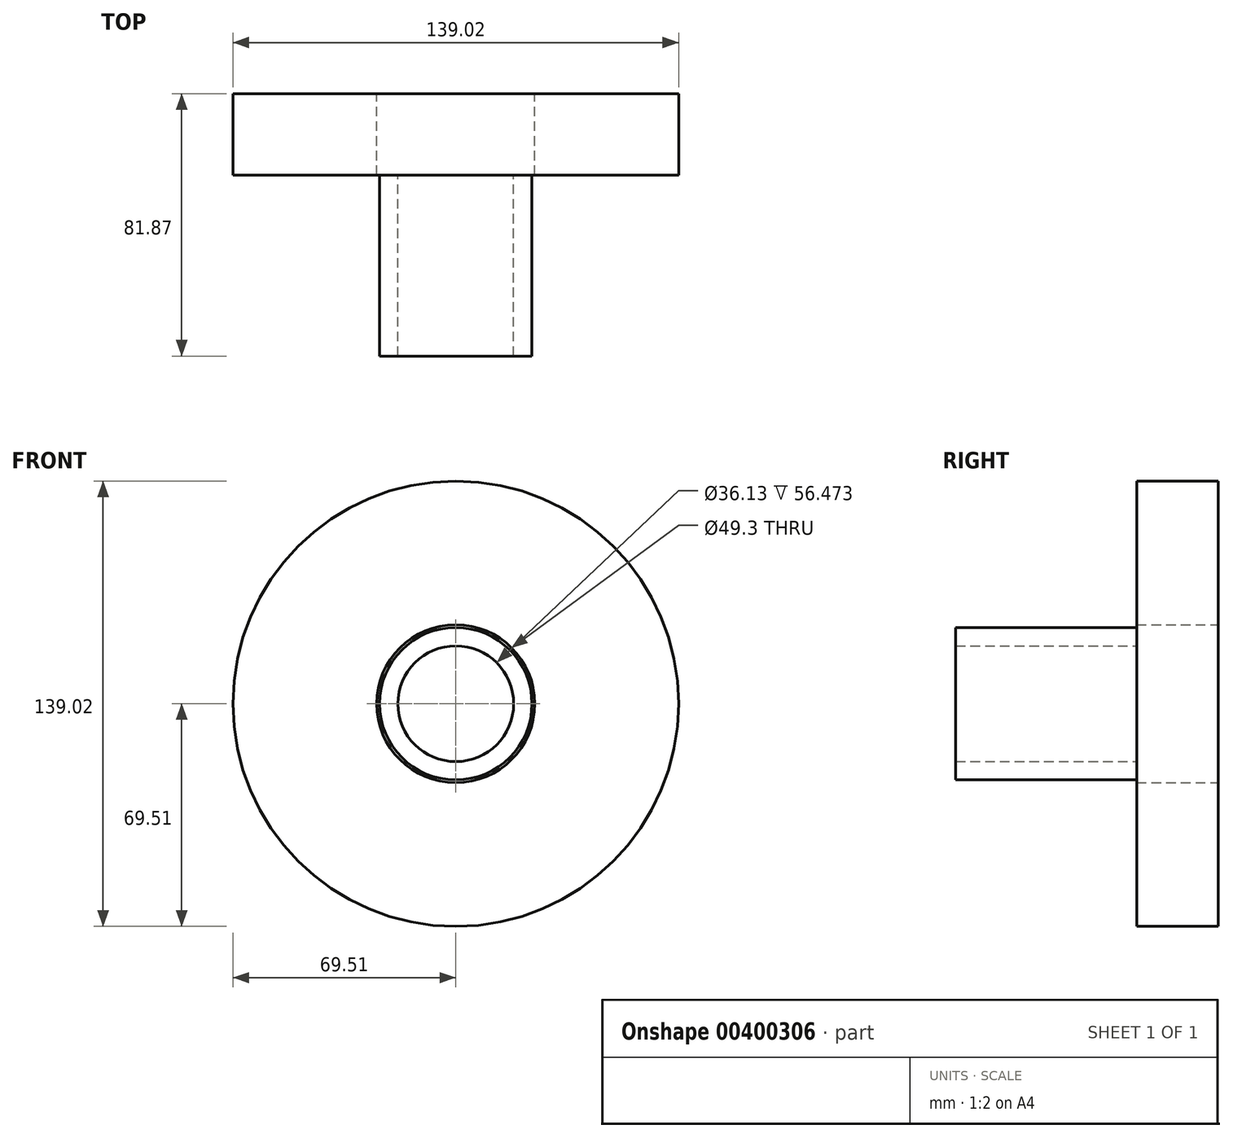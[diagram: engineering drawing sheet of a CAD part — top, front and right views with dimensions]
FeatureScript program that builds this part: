
annotation { "Feature Type Name" : "Feature", "Feature Type Description" : "" }
export const myFeature = defineFeature(function(context is Context, id is Id, definition is map)
    precondition{}
    {
        {
            var Q0;
            Q0=qCreatedBy(makeId("Front.planeOp"),FACE);
            var sketch = newSketch(context, id + "F0", { "sketchPlane" : qUnion([Q0])});
            skCircle(sketch, "E0", {"center": v(0, 0) * mm, "radius": 69.51 * mm});
            skCircle(sketch, "E1", {"center": v(0, 0) * mm, "radius": 24.65 * mm});
            skSolve(sketch);
        }
        {
            var Q0;
            Q0=makeQuery(id+"F0.imprint","IMPRINT",FACE,{"disambiguationData":[TD([[makeQuery(id+"F0.imprint","IMPRINT",EDGE,{"derivedFrom":sQuery(id+"F0.wireOp",EDGE,"E0")}),1.0]])]});
            var Q1;
            Q1 = qSketchRegion(id + "F0", true);
            extrude(context, id + "F1", {"entities" : qUnion([Q0, Q1]), "depth" : 25.4 * mm});
        }
        {
            var Q0;
            Q0=makeQuery(id+"F1.opExtrude","CAP_FACE",FACE,{"disambiguationData":[OSD([sQuery(id+"F0.wireOp",EDGE,"E0"),sQuery(id+"F0.wireOp",EDGE,"E1")])],"isStart":false});
            var sketch = newSketch(context, id + "F2", { "sketchPlane" : qUnion([Q0])});
            skCircle(sketch, "E2", {"center": v(0, 0) * mm, "radius": 23.78 * mm});
            skCircle(sketch, "E3", {"center": v(0, 0) * mm, "radius": 18.06 * mm});
            skSolve(sketch);
        }
        {
            var Q0;
            Q0 = qSketchRegion(id + "F2", true);
            extrude(context, id + "F3", {"entities" : qUnion([Q0]), "depth" : 56.47 * mm});
        }
    });
